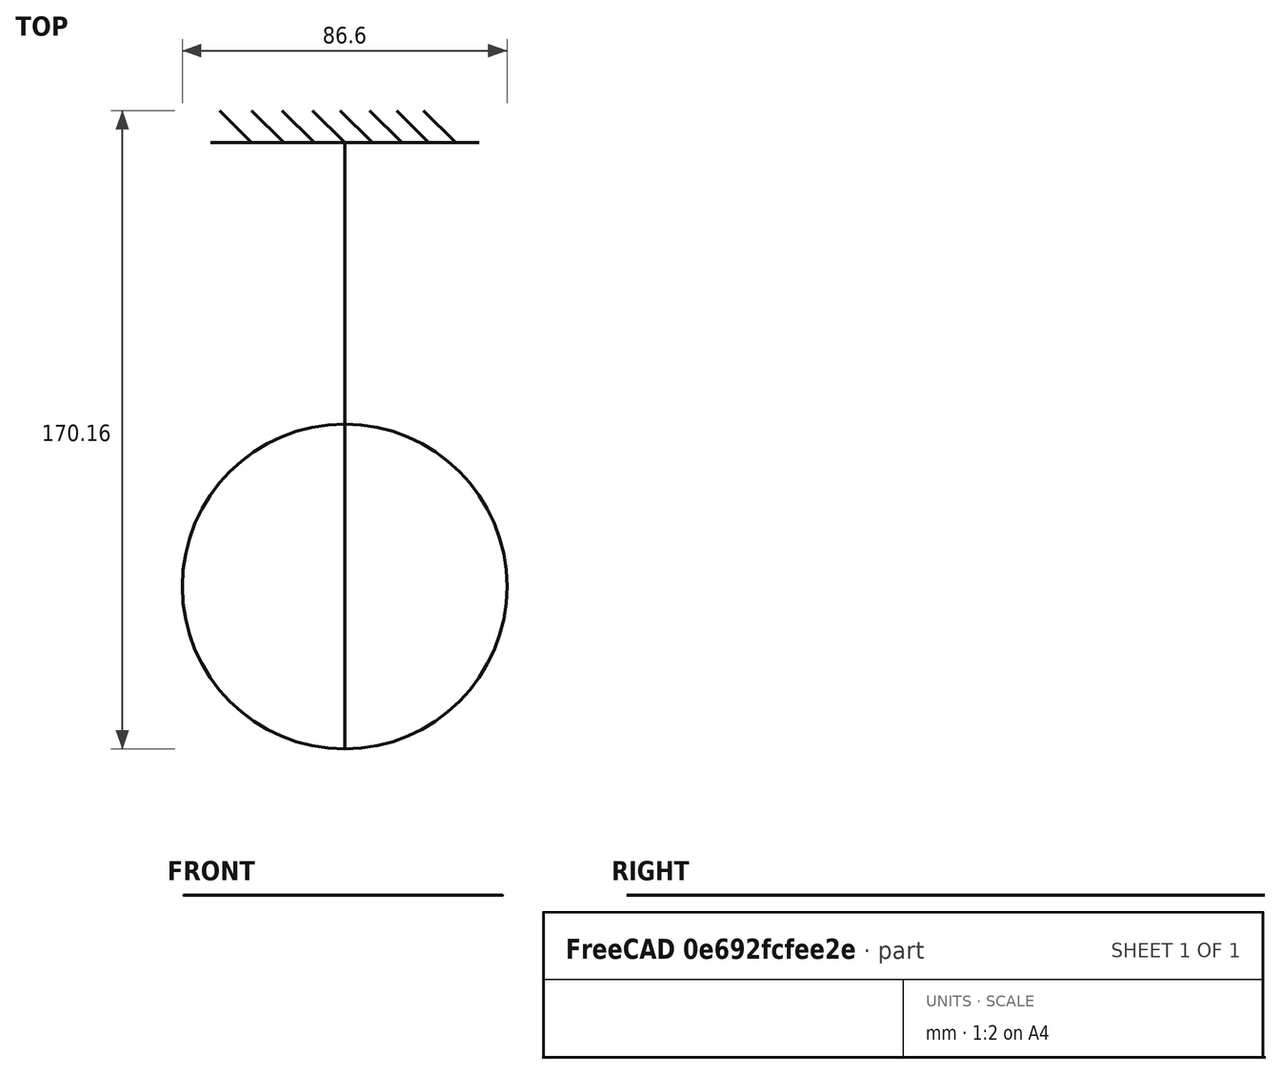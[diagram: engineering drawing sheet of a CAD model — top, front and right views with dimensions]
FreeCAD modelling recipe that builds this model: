
FCSTD DOCUMENT  (FreeCAD 1.1R20260325 (Git shallow))
Label: Conj_Tomada_Antena_Cabo_de_Rede
License: All rights reserved
LicenseURL: http://en.wikipedia.org/wiki/All_rights_reserved
objects: Part::FeaturePython×1, Part::Feature×1, App::DocumentObjectGroup×1
note: 2 computed .brp shape members not serialized (recipe doc carries the construction recipe); baked Part::Feature solids carry a one-line shape summary decoded from their .brp

FEATURE [Part::FeaturePython] Component  label="Rede ou Cabo Fibra001"  # Arch/BIM 0 (typed FeaturePython)
  HorizontalArea = 0
  IfcData = attributes={"GlobalId": {"name": "GlobalId", "type": "IfcGloballyUniqueId", "is_enum": false, "enum_values": []}, "Description": {"... (+538 chars omitted),+1 more (map truncated)
  IfcType = 0
  MoveBase = false
  MoveWithHost = false
  PerimeterLength = 0
  Placement = pos=(0,0,300) rot=(0,0,1;0rad)
  PredefinedType = 0
  VerticalArea = 0
FEATURE [Part::Feature] Compound002002002004005002002003003002003005002002005002002002002002002002002002002003  label="Simbologia_cabo_rede"
  shape: bbox 86.6 x 170.2 x 3e-07 mm, 1 faces, 0 solids (baked)
FEATURE [App::DocumentObjectGroup] Group  label="HRC_Rede ou Cabo Fibra"
  Group = -> [Compound002002002004005002002003003002003005002002005002002002002002002002002002002003,Component]
